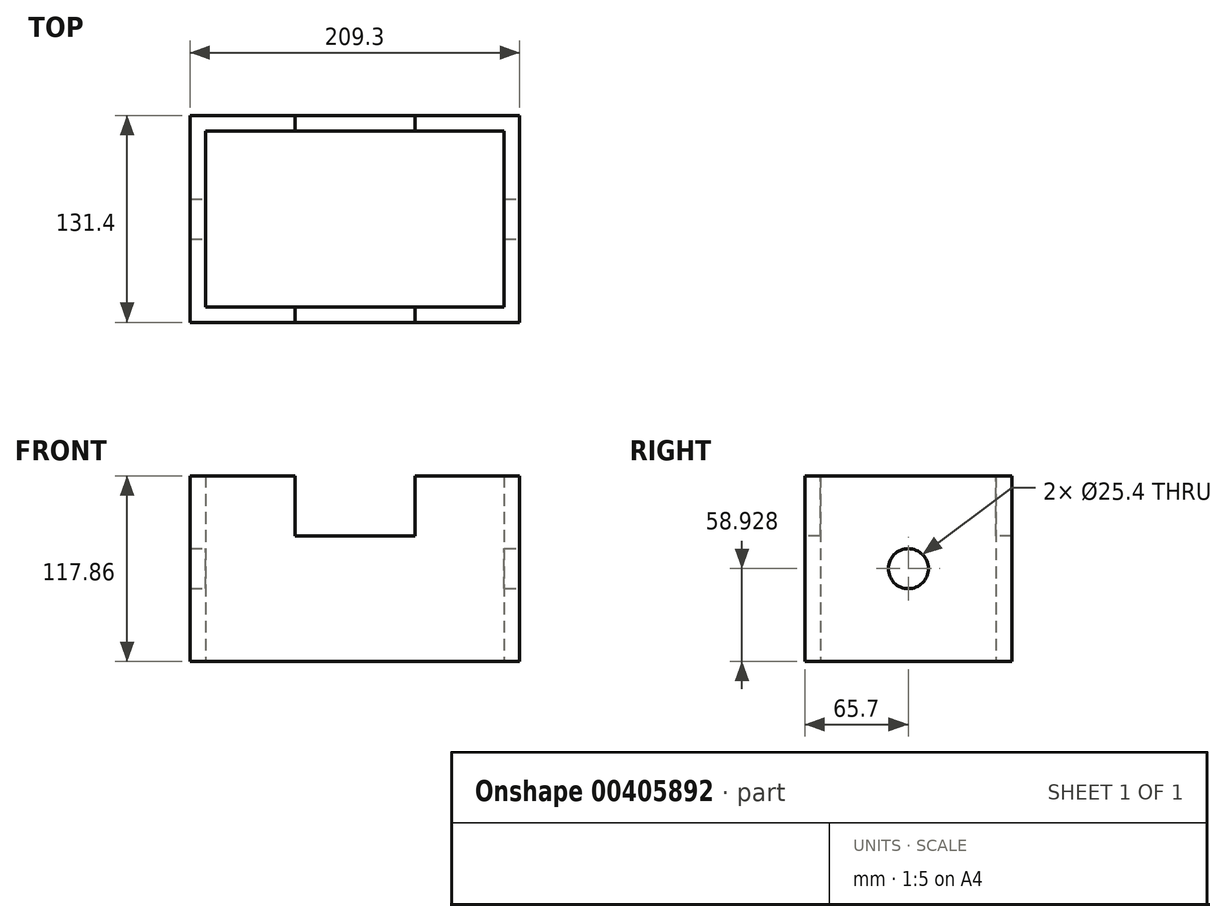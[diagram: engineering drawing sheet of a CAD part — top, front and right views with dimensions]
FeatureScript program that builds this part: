
annotation { "Feature Type Name" : "Feature", "Feature Type Description" : "" }
export const myFeature = defineFeature(function(context is Context, id is Id, definition is map)
    precondition{}
    {
        {
            var Q0;
            Q0=qCreatedBy(makeId("Top.planeOp"),FACE);
            var sketch = newSketch(context, id + "F0", { "sketchPlane" : qUnion([Q0])});
            skLineSegment(sketch, "E0.bottom", {"start": v(-104.65, 65.7) * mm, "end": v(104.65, 65.7) * mm});
            skLineSegment(sketch, "E0.top", {"start": v(-104.65, -65.7) * mm, "end": v(104.65, -65.7) * mm});
            skLineSegment(sketch, "E0.left", {"start": v(-104.65, 65.7) * mm, "end": v(-104.65, -65.7) * mm});
            skLineSegment(sketch, "E0.right", {"start": v(104.65, 65.7) * mm, "end": v(104.65, -65.7) * mm});
            skPoint(sketch, "E0.middle", {"position": v(0, 0) * mm});
            skLineSegment(sketch, "E1.0", {"start": v(-94.75, 55.8) * mm, "end": v(94.75, 55.8) * mm});
            skLineSegment(sketch, "E1.1", {"start": v(-94.75, 55.8) * mm, "end": v(-94.75, -55.8) * mm});
            skLineSegment(sketch, "E1.2", {"start": v(-94.75, -55.8) * mm, "end": v(94.75, -55.8) * mm});
            skLineSegment(sketch, "E1.3", {"start": v(94.75, 55.8) * mm, "end": v(94.75, -55.8) * mm});
            skSolve(sketch);
        }
        {
            var Q0;
            Q0=makeQuery(id+"F0.imprint","IMPRINT",FACE,{"disambiguationData":[TD([[makeQuery(id+"F0.imprint","IMPRINT",EDGE,{"derivedFrom":sQuery(id+"F0.wireOp",EDGE,"E0.bottom")}),-1.0]])]});
            extrude(context, id + "F1", {"entities" : qUnion([Q0]), "depth" : 117.86 * mm});
        }
        {
            var Q0;
            Q0=makeQuery(id+"F1.opExtrude","CAP_FACE",FACE,{"disambiguationData":[OSD([sQuery(id+"F0.wireOp",EDGE,"E0.bottom"),sQuery(id+"F0.wireOp",EDGE,"E0.top"),sQuery(id+"F0.wireOp",EDGE,"E0.left"),sQuery(id+"F0.wireOp",EDGE,"E0.right"),sQuery(id+"F0.wireOp",EDGE,"E1.0"),sQuery(id+"F0.wireOp",EDGE,"E1.1"),sQuery(id+"F0.wireOp",EDGE,"E1.2"),sQuery(id+"F0.wireOp",EDGE,"E1.3")])],"isStart":false});
            var sketch = newSketch(context, id + "F2", { "sketchPlane" : qUnion([Q0])});
            skLineSegment(sketch, "E2.bottom", {"start": v(-38.1, 146.83) * mm, "end": v(38.1, 146.83) * mm});
            skLineSegment(sketch, "E2.top", {"start": v(-38.1, -146.83) * mm, "end": v(38.1, -146.83) * mm});
            skLineSegment(sketch, "E2.left", {"start": v(-38.1, 146.83) * mm, "end": v(-38.1, -146.83) * mm});
            skLineSegment(sketch, "E2.right", {"start": v(38.1, 146.83) * mm, "end": v(38.1, -146.83) * mm});
            skPoint(sketch, "E2.middle", {"position": v(0, 0) * mm});
            skSolve(sketch);
        }
        {
            var Q0;
            {var subQ0=sQuery(id+"F2.wireOp",EDGE,"E2.left");var subQ1=makeQuery(id+"F1.opExtrude","CAP_EDGE",EDGE,{"disambiguationData":[OSD([sQuery(id+"F0.wireOp",EDGE,"E0.bottom")])],"isStart":false});var subQ2=makeQuery(id+"F2.imprint","INTERSECT",VERTEX,{"derivedFrom":[subQ1,subQ0]});Q0=makeQuery(id+"F2.imprint","IMPRINT",FACE,{"disambiguationData":[TD([[makeQuery(id+"F2.imprint","IMPRINT",EDGE,{"disambiguationData":[TD([[subQ2,-1.0]])],"derivedFrom":subQ0}),1.0]])]});}
            var Q1;
            {var subQ0=sQuery(id+"F2.wireOp",EDGE,"E2.left");var subQ1=makeQuery(id+"F1.opExtrude","CAP_EDGE",EDGE,{"disambiguationData":[OSD([sQuery(id+"F0.wireOp",EDGE,"E0.top")])],"isStart":false});var subQ2=makeQuery(id+"F2.imprint","INTERSECT",VERTEX,{"derivedFrom":[subQ1,subQ0]});Q1=makeQuery(id+"F2.imprint","IMPRINT",FACE,{"disambiguationData":[TD([[makeQuery(id+"F2.imprint","IMPRINT",EDGE,{"disambiguationData":[TD([[subQ2,1.0]])],"derivedFrom":subQ0}),1.0]])]});}
            extrude(context, id + "F3", {"entities" : qUnion([Q0, Q1]), "operationType" : NewBodyOperationType.REMOVE, "oppositeDirection" : true, "depth" : 38.1 * mm});
        }
        {
            var Q0;
            Q0=makeQuery(id+"F1.opExtrude","SWEPT_FACE",FACE,{"disambiguationData":[OSD([sQuery(id+"F0.wireOp",EDGE,"E0.right")])]});
            var sketch = newSketch(context, id + "F4", { "sketchPlane" : qUnion([Q0])});
            skCircle(sketch, "E3", {"center": v(0, 58.93) * mm, "radius": 12.7 * mm});
            skPoint(sketch, "E3.centerSnap0", {"position": v(-65.7, 58.93) * mm});
            skSolve(sketch);
        }
        {
            var Q0;
            Q0=makeQuery(id+"F4.imprint","IMPRINT",FACE,{"disambiguationData":[TD([[makeQuery(id+"F4.imprint","IMPRINT",EDGE,{"derivedFrom":sQuery(id+"F4.wireOp",EDGE,"E3")}),1.0]])]});
            extrude(context, id + "F5", {"entities" : qUnion([Q0]), "operationType" : NewBodyOperationType.REMOVE, "endBound" : BoundingType.THROUGH_ALL, "oppositeDirection" : true, "depth" : 25.4 * mm});
        }
    });
